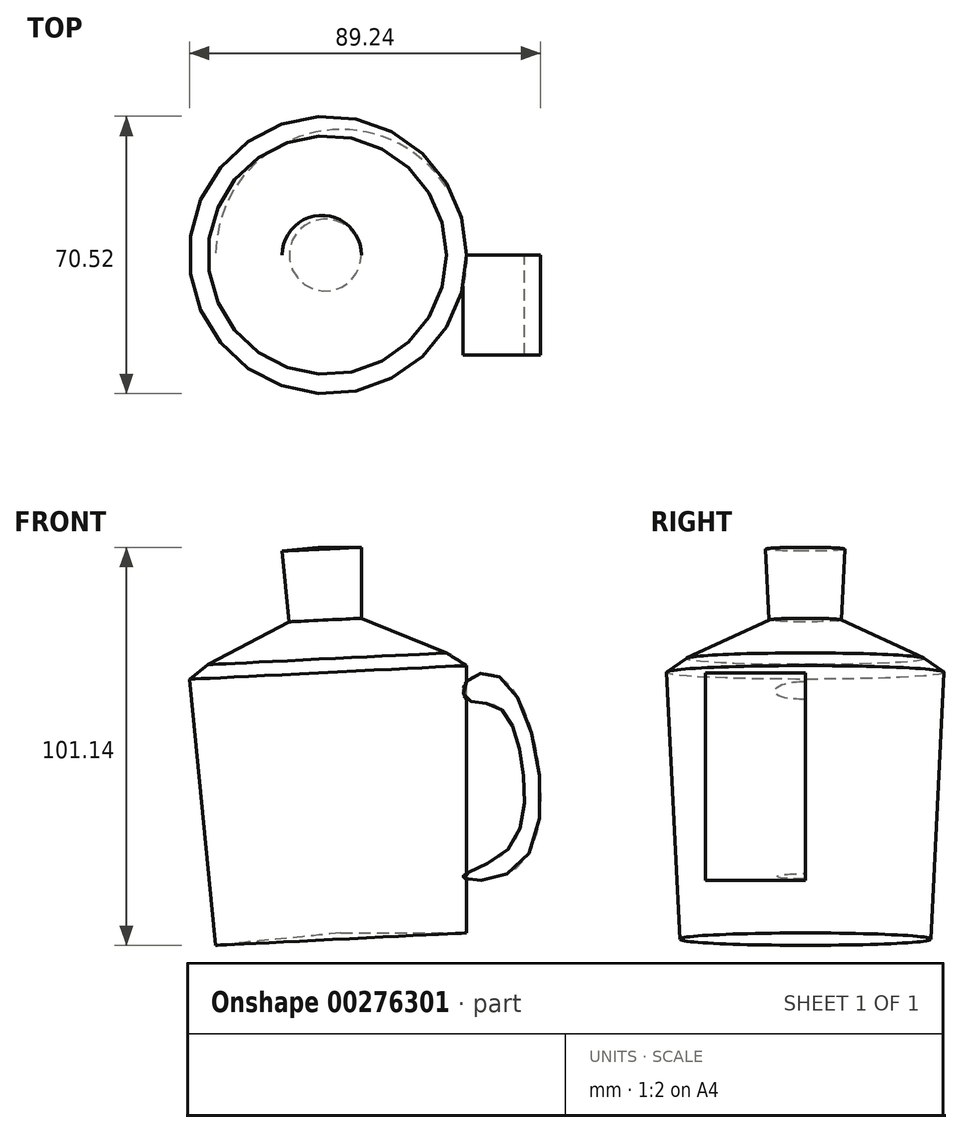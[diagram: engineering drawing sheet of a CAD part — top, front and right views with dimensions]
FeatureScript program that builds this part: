
annotation { "Feature Type Name" : "Feature", "Feature Type Description" : "" }
export const myFeature = defineFeature(function(context is Context, id is Id, definition is map)
    precondition{}
    {
        {
            var Q0;
            Q0=qCreatedBy(makeId("Front.planeOp"),FACE);
            var sketch = newSketch(context, id + "F0", { "sketchPlane" : qUnion([Q0])});
            skLineSegment(sketch, "E0", {"start": v(0, -35.7) * mm, "end": v(31.95, -35.7) * mm});
            skLineSegment(sketch, "E1", {"start": v(31.95, -35.7) * mm, "end": v(31.95, 32.22) * mm});
            skLineSegment(sketch, "E2", {"start": v(26.85, 35.44) * mm, "end": v(31.95, 32.22) * mm});
            skLineSegment(sketch, "E3", {"start": v(12.35, 41.35) * mm, "end": v(26.85, 35.44) * mm});
            skLineSegment(sketch, "E4", {"start": v(12.35, 41.35) * mm, "end": v(5.25, 44.24) * mm});
            skLineSegment(sketch, "E5", {"start": v(5.25, 44.24) * mm, "end": v(5.25, 62.29) * mm});
            skLineSegment(sketch, "E6", {"start": v(5.25, 62.29) * mm, "end": v(-4.83, 62.29) * mm});
            skLineSegment(sketch, "E7", {"start": v(-4.83, 62.29) * mm, "end": v(0, -35.7) * mm});
            skSolve(sketch);
        }
        {
            var Q0;
            Q0=makeQuery(id+"F0.imprint","IMPRINT",FACE,{"disambiguationData":[TD([[makeQuery(id+"F0.imprint","IMPRINT",EDGE,{"derivedFrom":sQuery(id+"F0.wireOp",EDGE,"E0")}),1.0]])]});
            var Q1;
            Q1=sQuery(id+"F0.wireOp",EDGE,"E7");
            revolve(context, id + "F1", {"entities" : qUnion([Q0]), "axis" : qUnion([Q1]), "revolveType" : RevolveType.FULL});
        }
        {
            var Q0;
            Q0=qCreatedBy(makeId("Front.planeOp"),FACE);
            var sketch = newSketch(context, id + "F2", { "sketchPlane" : qUnion([Q0])});
            skFitSpline(sketch, "E8", {"points": [v(31.95, 28.2) * mm, v(41.88, 28.2) * mm, v(46.18, -17.72) * mm, v(31.14, -21.48) * mm, v(41.88, -15.04) * mm, v(46.18, 6.44) * mm, v(39.74, 21.75) * mm, v(31.95, 23.63) * mm, v(31.95, 28.2) * mm]});
            skSolve(sketch);
        }
        {
            var Q0;
            Q0=makeQuery(id+"F2.imprint","IMPRINT",FACE,{"disambiguationData":[TD([[makeQuery(id+"F2.imprint","IMPRINT",EDGE,{"derivedFrom":sQuery(id+"F2.wireOp",EDGE,"E8")}),-1.0]])]});
            extrude(context, id + "F3", {"entities" : qUnion([Q0]), "operationType" : NewBodyOperationType.ADD, "depth" : 25.4 * mm});
        }
    });
